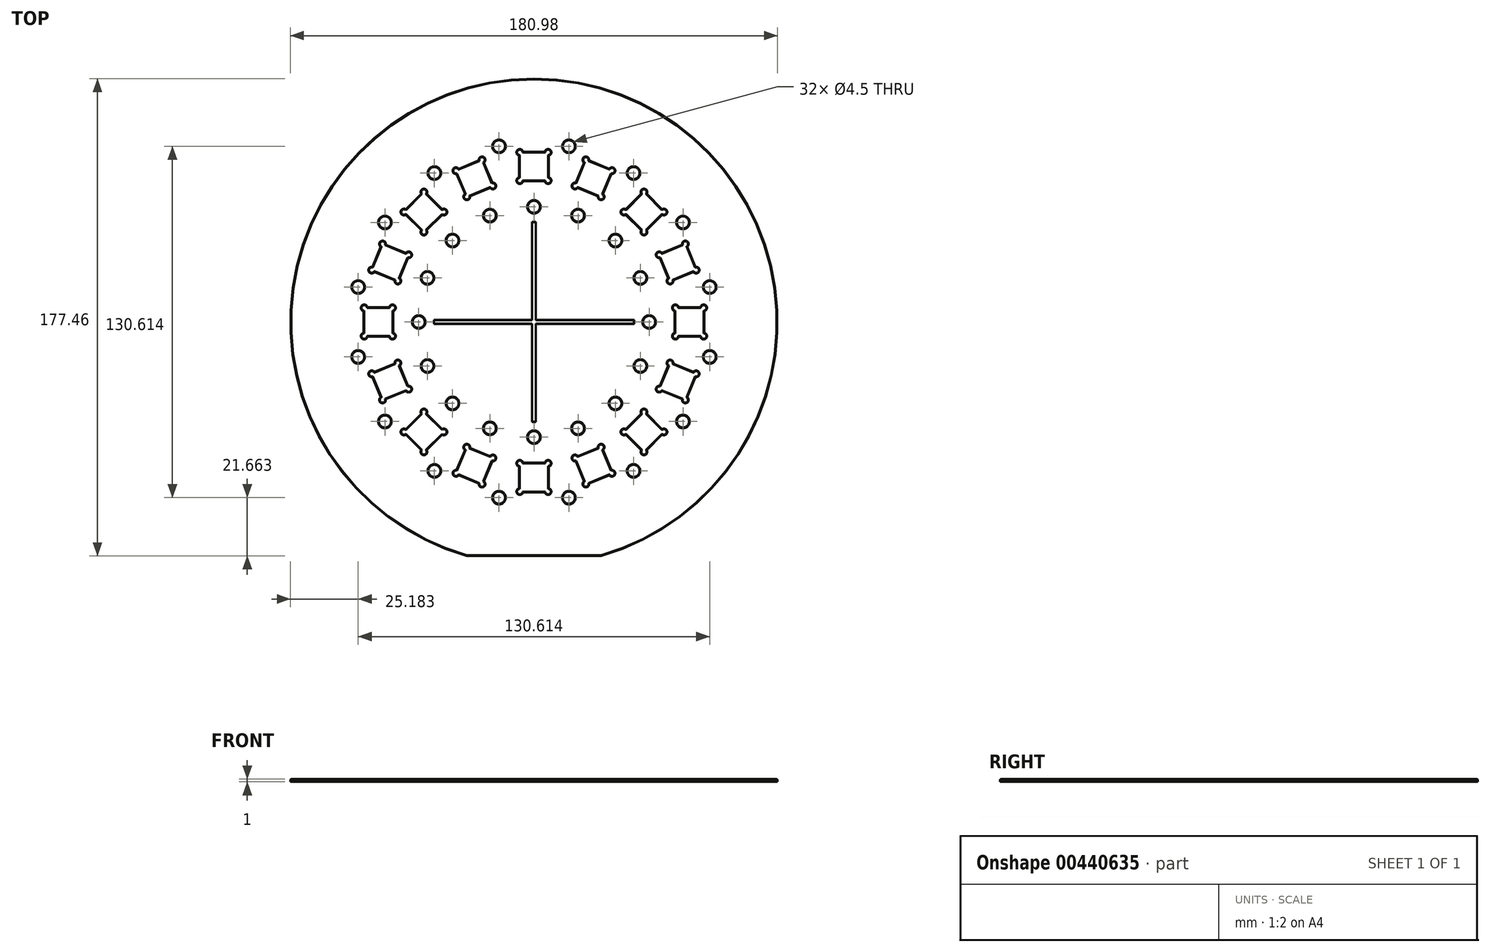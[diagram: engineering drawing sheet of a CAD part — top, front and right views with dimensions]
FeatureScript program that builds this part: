
annotation { "Feature Type Name" : "Feature", "Feature Type Description" : "" }
export const myFeature = defineFeature(function(context is Context, id is Id, definition is map)
    precondition{}
    {
        {
            var Q0;
            Q0=qCreatedBy(makeId("Top.planeOp"),FACE);
            var sketch = newSketch(context, id + "F0", { "sketchPlane" : qUnion([Q0])});
            skArc(sketch, "E0", {"start": v(25, -86.97) * mm, "mid": v(0, 90.49) * mm, "end": v(-25, -86.97) * mm});
            skCircle(sketch, "E1", {"center": v(0, 0) * mm, "radius": 57.8 * mm, "construction": true});
            skLineSegment(sketch, "E2.bottom", {"start": v(5.25, 63.06) * mm, "end": v(-5.25, 63.06) * mm});
            skLineSegment(sketch, "E2.top", {"start": v(5.25, 52.56) * mm, "end": v(-5.25, 52.56) * mm});
            skLineSegment(sketch, "E2.left", {"start": v(5.25, 63.06) * mm, "end": v(5.25, 52.56) * mm});
            skLineSegment(sketch, "E2.right", {"start": v(-5.25, 63.06) * mm, "end": v(-5.25, 52.56) * mm});
            skPoint(sketch, "E2.middle", {"position": v(0, 57.8) * mm});
            skCircle(sketch, "E3", {"center": v(0, 42.8) * mm, "radius": 2.25 * mm});
            skLineSegment(sketch, "E4", {"start": v(0, 42.8) * mm, "end": v(0, 57.8) * mm, "construction": true});
            skCircle(sketch, "E5.1.0", {"center": v(13, 65.3) * mm, "radius": 2.25 * mm, "construction": true});
            skCircle(sketch, "E5.2.0", {"center": v(-13, 65.3) * mm, "radius": 2.25 * mm});
            skCircle(sketch, "E6", {"center": v(-5.25, 63.06) * mm, "radius": 1 * mm});
            skCircle(sketch, "E7", {"center": v(5.25, 63.06) * mm, "radius": 1 * mm});
            skCircle(sketch, "E8", {"center": v(5.25, 52.56) * mm, "radius": 1 * mm});
            skCircle(sketch, "E9", {"center": v(-5.25, 52.56) * mm, "radius": 1 * mm});
            skLineSegment(sketch, "E10.1.0", {"start": v(-19.28, 60.27) * mm, "end": v(-15.26, 50.57) * mm});
            skLineSegment(sketch, "E10.1.1", {"start": v(-28.98, 56.25) * mm, "end": v(-24.96, 46.55) * mm});
            skPoint(sketch, "E10.1.2", {"position": v(-22.12, 53.4) * mm});
            skCircle(sketch, "E10.1.3", {"center": v(-16.38, 39.55) * mm, "radius": 2.25 * mm});
            skLineSegment(sketch, "E10.1.4", {"start": v(-15.26, 50.57) * mm, "end": v(-24.96, 46.55) * mm});
            skCircle(sketch, "E10.1.5", {"center": v(-13, 65.3) * mm, "radius": 2.25 * mm, "construction": true});
            skLineSegment(sketch, "E10.1.6", {"start": v(-16.38, 39.55) * mm, "end": v(-22.12, 53.4) * mm, "construction": true});
            skCircle(sketch, "E10.1.7", {"center": v(-37, 55.36) * mm, "radius": 2.25 * mm});
            skLineSegment(sketch, "E10.1.8", {"start": v(-19.28, 60.27) * mm, "end": v(-28.98, 56.25) * mm});
            skPoint(sketch, "E10.1.9", {"position": v(-22.12, 53.4) * mm});
            skCircle(sketch, "E10.1.10", {"center": v(-19.28, 60.27) * mm, "radius": 1 * mm});
            skCircle(sketch, "E10.1.11", {"center": v(-15.26, 50.57) * mm, "radius": 1 * mm});
            skCircle(sketch, "E10.1.12", {"center": v(-24.96, 46.55) * mm, "radius": 1 * mm});
            skCircle(sketch, "E10.1.13", {"center": v(-28.98, 56.25) * mm, "radius": 1 * mm});
            skLineSegment(sketch, "E10.2.0", {"start": v(-40.88, 48.3) * mm, "end": v(-33.45, 40.88) * mm});
            skLineSegment(sketch, "E10.2.1", {"start": v(-48.3, 40.88) * mm, "end": v(-40.88, 33.45) * mm});
            skPoint(sketch, "E10.2.2", {"position": v(-40.88, 40.88) * mm});
            skCircle(sketch, "E10.2.3", {"center": v(-30.27, 30.27) * mm, "radius": 2.25 * mm});
            skLineSegment(sketch, "E10.2.4", {"start": v(-33.45, 40.88) * mm, "end": v(-40.88, 33.45) * mm});
            skCircle(sketch, "E10.2.5", {"center": v(-37, 55.36) * mm, "radius": 2.25 * mm, "construction": true});
            skLineSegment(sketch, "E10.2.6", {"start": v(-30.27, 30.27) * mm, "end": v(-40.88, 40.88) * mm, "construction": true});
            skCircle(sketch, "E10.2.7", {"center": v(-55.36, 37) * mm, "radius": 2.25 * mm});
            skLineSegment(sketch, "E10.2.8", {"start": v(-40.88, 48.3) * mm, "end": v(-48.3, 40.88) * mm});
            skPoint(sketch, "E10.2.9", {"position": v(-40.88, 40.88) * mm});
            skCircle(sketch, "E10.2.10", {"center": v(-40.88, 48.3) * mm, "radius": 1 * mm});
            skCircle(sketch, "E10.2.11", {"center": v(-33.45, 40.88) * mm, "radius": 1 * mm});
            skCircle(sketch, "E10.2.12", {"center": v(-40.88, 33.45) * mm, "radius": 1 * mm});
            skCircle(sketch, "E10.2.13", {"center": v(-48.3, 40.88) * mm, "radius": 1 * mm});
            skLineSegment(sketch, "E11.3.3.0", {"start": v(-60.27, 19.28) * mm, "end": v(-50.57, 15.26) * mm});
            skPoint(sketch, "E11.6.3.0", {"position": v(-53.4, 22.12) * mm});
            skCircle(sketch, "E11.7.3.0", {"center": v(-39.55, 16.38) * mm, "radius": 2.25 * mm});
            skLineSegment(sketch, "E11.8.3.0", {"start": v(-56.25, 28.98) * mm, "end": v(-46.55, 24.96) * mm});
            skLineSegment(sketch, "E11.9.3.0", {"start": v(-46.55, 24.96) * mm, "end": v(-50.57, 15.26) * mm});
            skCircle(sketch, "E11.12.3.0", {"center": v(-55.36, 37) * mm, "radius": 2.25 * mm, "construction": true});
            skLineSegment(sketch, "E11.14.3.0", {"start": v(-39.55, 16.38) * mm, "end": v(-53.4, 22.12) * mm, "construction": true});
            skCircle(sketch, "E11.17.3.0", {"center": v(-65.3, 13) * mm, "radius": 2.25 * mm});
            skLineSegment(sketch, "E11.19.3.0", {"start": v(-56.25, 28.98) * mm, "end": v(-60.27, 19.28) * mm});
            skPoint(sketch, "E11.22.3.0", {"position": v(-53.4, 22.12) * mm});
            skCircle(sketch, "E11.23.3.0", {"center": v(-56.25, 28.98) * mm, "radius": 1 * mm});
            skCircle(sketch, "E11.25.3.0", {"center": v(-46.55, 24.96) * mm, "radius": 1 * mm});
            skCircle(sketch, "E11.27.3.0", {"center": v(-50.57, 15.26) * mm, "radius": 1 * mm});
            skCircle(sketch, "E11.29.3.0", {"center": v(-60.27, 19.28) * mm, "radius": 1 * mm});
            skLineSegment(sketch, "E11.3.4.0", {"start": v(-63.06, -5.25) * mm, "end": v(-52.56, -5.25) * mm});
            skPoint(sketch, "E11.6.4.0", {"position": v(-57.8, 0) * mm});
            skCircle(sketch, "E11.7.4.0", {"center": v(-42.8, 0) * mm, "radius": 2.25 * mm});
            skLineSegment(sketch, "E11.8.4.0", {"start": v(-63.06, 5.25) * mm, "end": v(-52.56, 5.25) * mm});
            skLineSegment(sketch, "E11.9.4.0", {"start": v(-52.56, 5.25) * mm, "end": v(-52.56, -5.25) * mm});
            skCircle(sketch, "E11.12.4.0", {"center": v(-65.3, 13) * mm, "radius": 2.25 * mm, "construction": true});
            skLineSegment(sketch, "E11.14.4.0", {"start": v(-42.8, 0) * mm, "end": v(-57.8, 0) * mm, "construction": true});
            skCircle(sketch, "E11.17.4.0", {"center": v(-65.3, -13) * mm, "radius": 2.25 * mm});
            skLineSegment(sketch, "E11.19.4.0", {"start": v(-63.06, 5.25) * mm, "end": v(-63.06, -5.25) * mm});
            skPoint(sketch, "E11.22.4.0", {"position": v(-57.8, 0) * mm});
            skCircle(sketch, "E11.23.4.0", {"center": v(-63.06, 5.25) * mm, "radius": 1 * mm});
            skCircle(sketch, "E11.25.4.0", {"center": v(-52.56, 5.25) * mm, "radius": 1 * mm});
            skCircle(sketch, "E11.27.4.0", {"center": v(-52.56, -5.25) * mm, "radius": 1 * mm});
            skCircle(sketch, "E11.29.4.0", {"center": v(-63.06, -5.25) * mm, "radius": 1 * mm});
            skLineSegment(sketch, "E11.3.5.0", {"start": v(-56.25, -28.98) * mm, "end": v(-46.55, -24.96) * mm});
            skPoint(sketch, "E11.6.5.0", {"position": v(-53.4, -22.12) * mm});
            skCircle(sketch, "E11.7.5.0", {"center": v(-39.55, -16.38) * mm, "radius": 2.25 * mm});
            skLineSegment(sketch, "E11.8.5.0", {"start": v(-60.27, -19.28) * mm, "end": v(-50.57, -15.26) * mm});
            skLineSegment(sketch, "E11.9.5.0", {"start": v(-50.57, -15.26) * mm, "end": v(-46.55, -24.96) * mm});
            skCircle(sketch, "E11.12.5.0", {"center": v(-65.3, -13) * mm, "radius": 2.25 * mm, "construction": true});
            skLineSegment(sketch, "E11.14.5.0", {"start": v(-39.55, -16.38) * mm, "end": v(-53.4, -22.12) * mm, "construction": true});
            skCircle(sketch, "E11.17.5.0", {"center": v(-55.36, -37) * mm, "radius": 2.25 * mm});
            skLineSegment(sketch, "E11.19.5.0", {"start": v(-60.27, -19.28) * mm, "end": v(-56.25, -28.98) * mm});
            skPoint(sketch, "E11.22.5.0", {"position": v(-53.4, -22.12) * mm});
            skCircle(sketch, "E11.23.5.0", {"center": v(-60.27, -19.28) * mm, "radius": 1 * mm});
            skCircle(sketch, "E11.25.5.0", {"center": v(-50.57, -15.26) * mm, "radius": 1 * mm});
            skCircle(sketch, "E11.27.5.0", {"center": v(-46.55, -24.96) * mm, "radius": 1 * mm});
            skCircle(sketch, "E11.29.5.0", {"center": v(-56.25, -28.98) * mm, "radius": 1 * mm});
            skLineSegment(sketch, "E11.3.6.0", {"start": v(-40.88, -48.3) * mm, "end": v(-33.45, -40.88) * mm});
            skPoint(sketch, "E11.6.6.0", {"position": v(-40.88, -40.88) * mm});
            skCircle(sketch, "E11.7.6.0", {"center": v(-30.27, -30.27) * mm, "radius": 2.25 * mm});
            skLineSegment(sketch, "E11.8.6.0", {"start": v(-48.3, -40.88) * mm, "end": v(-40.88, -33.45) * mm});
            skLineSegment(sketch, "E11.9.6.0", {"start": v(-40.88, -33.45) * mm, "end": v(-33.45, -40.88) * mm});
            skCircle(sketch, "E11.12.6.0", {"center": v(-55.36, -37) * mm, "radius": 2.25 * mm, "construction": true});
            skLineSegment(sketch, "E11.14.6.0", {"start": v(-30.27, -30.27) * mm, "end": v(-40.88, -40.88) * mm, "construction": true});
            skCircle(sketch, "E11.17.6.0", {"center": v(-37, -55.36) * mm, "radius": 2.25 * mm});
            skLineSegment(sketch, "E11.19.6.0", {"start": v(-48.3, -40.88) * mm, "end": v(-40.88, -48.3) * mm});
            skPoint(sketch, "E11.22.6.0", {"position": v(-40.88, -40.88) * mm});
            skCircle(sketch, "E11.23.6.0", {"center": v(-48.3, -40.88) * mm, "radius": 1 * mm});
            skCircle(sketch, "E11.25.6.0", {"center": v(-40.88, -33.45) * mm, "radius": 1 * mm});
            skCircle(sketch, "E11.27.6.0", {"center": v(-33.45, -40.88) * mm, "radius": 1 * mm});
            skCircle(sketch, "E11.29.6.0", {"center": v(-40.88, -48.3) * mm, "radius": 1 * mm});
            skLineSegment(sketch, "E11.3.7.0", {"start": v(-19.28, -60.27) * mm, "end": v(-15.26, -50.57) * mm});
            skPoint(sketch, "E11.6.7.0", {"position": v(-22.12, -53.4) * mm});
            skCircle(sketch, "E11.7.7.0", {"center": v(-16.38, -39.55) * mm, "radius": 2.25 * mm});
            skLineSegment(sketch, "E11.8.7.0", {"start": v(-28.98, -56.25) * mm, "end": v(-24.96, -46.55) * mm});
            skLineSegment(sketch, "E11.9.7.0", {"start": v(-24.96, -46.55) * mm, "end": v(-15.26, -50.57) * mm});
            skCircle(sketch, "E11.12.7.0", {"center": v(-37, -55.36) * mm, "radius": 2.25 * mm, "construction": true});
            skLineSegment(sketch, "E11.14.7.0", {"start": v(-16.38, -39.55) * mm, "end": v(-22.12, -53.4) * mm, "construction": true});
            skCircle(sketch, "E11.17.7.0", {"center": v(-13, -65.3) * mm, "radius": 2.25 * mm});
            skLineSegment(sketch, "E11.19.7.0", {"start": v(-28.98, -56.25) * mm, "end": v(-19.28, -60.27) * mm});
            skPoint(sketch, "E11.22.7.0", {"position": v(-22.12, -53.4) * mm});
            skCircle(sketch, "E11.23.7.0", {"center": v(-28.98, -56.25) * mm, "radius": 1 * mm});
            skCircle(sketch, "E11.25.7.0", {"center": v(-24.96, -46.55) * mm, "radius": 1 * mm});
            skCircle(sketch, "E11.27.7.0", {"center": v(-15.26, -50.57) * mm, "radius": 1 * mm});
            skCircle(sketch, "E11.29.7.0", {"center": v(-19.28, -60.27) * mm, "radius": 1 * mm});
            skLineSegment(sketch, "E11.3.8.0", {"start": v(5.25, -63.06) * mm, "end": v(5.25, -52.56) * mm});
            skPoint(sketch, "E11.6.8.0", {"position": v(0, -57.8) * mm});
            skCircle(sketch, "E11.7.8.0", {"center": v(0, -42.8) * mm, "radius": 2.25 * mm});
            skLineSegment(sketch, "E11.8.8.0", {"start": v(-5.25, -63.06) * mm, "end": v(-5.25, -52.56) * mm});
            skLineSegment(sketch, "E11.9.8.0", {"start": v(-5.25, -52.56) * mm, "end": v(5.25, -52.56) * mm});
            skCircle(sketch, "E11.12.8.0", {"center": v(-13, -65.3) * mm, "radius": 2.25 * mm, "construction": true});
            skLineSegment(sketch, "E11.14.8.0", {"start": v(0, -42.8) * mm, "end": v(0, -57.8) * mm, "construction": true});
            skCircle(sketch, "E11.17.8.0", {"center": v(13, -65.3) * mm, "radius": 2.25 * mm});
            skLineSegment(sketch, "E11.19.8.0", {"start": v(-5.25, -63.06) * mm, "end": v(5.25, -63.06) * mm});
            skPoint(sketch, "E11.22.8.0", {"position": v(0, -57.8) * mm});
            skCircle(sketch, "E11.23.8.0", {"center": v(-5.25, -63.06) * mm, "radius": 1 * mm});
            skCircle(sketch, "E11.25.8.0", {"center": v(-5.25, -52.56) * mm, "radius": 1 * mm});
            skCircle(sketch, "E11.27.8.0", {"center": v(5.25, -52.56) * mm, "radius": 1 * mm});
            skCircle(sketch, "E11.29.8.0", {"center": v(5.25, -63.06) * mm, "radius": 1 * mm});
            skLineSegment(sketch, "E11.3.9.0", {"start": v(28.98, -56.25) * mm, "end": v(24.96, -46.55) * mm});
            skPoint(sketch, "E11.6.9.0", {"position": v(22.12, -53.4) * mm});
            skCircle(sketch, "E11.7.9.0", {"center": v(16.38, -39.55) * mm, "radius": 2.25 * mm});
            skLineSegment(sketch, "E11.8.9.0", {"start": v(19.28, -60.27) * mm, "end": v(15.26, -50.57) * mm});
            skLineSegment(sketch, "E11.9.9.0", {"start": v(15.26, -50.57) * mm, "end": v(24.96, -46.55) * mm});
            skCircle(sketch, "E11.12.9.0", {"center": v(13, -65.3) * mm, "radius": 2.25 * mm, "construction": true});
            skLineSegment(sketch, "E11.14.9.0", {"start": v(16.38, -39.55) * mm, "end": v(22.12, -53.4) * mm, "construction": true});
            skCircle(sketch, "E11.17.9.0", {"center": v(37, -55.36) * mm, "radius": 2.25 * mm});
            skLineSegment(sketch, "E11.19.9.0", {"start": v(19.28, -60.27) * mm, "end": v(28.98, -56.25) * mm});
            skPoint(sketch, "E11.22.9.0", {"position": v(22.12, -53.4) * mm});
            skCircle(sketch, "E11.23.9.0", {"center": v(19.28, -60.27) * mm, "radius": 1 * mm});
            skCircle(sketch, "E11.25.9.0", {"center": v(15.26, -50.57) * mm, "radius": 1 * mm});
            skCircle(sketch, "E11.27.9.0", {"center": v(24.96, -46.55) * mm, "radius": 1 * mm});
            skCircle(sketch, "E11.29.9.0", {"center": v(28.98, -56.25) * mm, "radius": 1 * mm});
            skLineSegment(sketch, "E11.3.10.0", {"start": v(48.3, -40.88) * mm, "end": v(40.88, -33.45) * mm});
            skPoint(sketch, "E11.6.10.0", {"position": v(40.88, -40.88) * mm});
            skCircle(sketch, "E11.7.10.0", {"center": v(30.27, -30.27) * mm, "radius": 2.25 * mm});
            skLineSegment(sketch, "E11.8.10.0", {"start": v(40.88, -48.3) * mm, "end": v(33.45, -40.88) * mm});
            skLineSegment(sketch, "E11.9.10.0", {"start": v(33.45, -40.88) * mm, "end": v(40.88, -33.45) * mm});
            skCircle(sketch, "E11.12.10.0", {"center": v(37, -55.36) * mm, "radius": 2.25 * mm, "construction": true});
            skLineSegment(sketch, "E11.14.10.0", {"start": v(30.27, -30.27) * mm, "end": v(40.88, -40.88) * mm, "construction": true});
            skCircle(sketch, "E11.17.10.0", {"center": v(55.36, -37) * mm, "radius": 2.25 * mm});
            skLineSegment(sketch, "E11.19.10.0", {"start": v(40.88, -48.3) * mm, "end": v(48.3, -40.88) * mm});
            skPoint(sketch, "E11.22.10.0", {"position": v(40.88, -40.88) * mm});
            skCircle(sketch, "E11.23.10.0", {"center": v(40.88, -48.3) * mm, "radius": 1 * mm});
            skCircle(sketch, "E11.25.10.0", {"center": v(33.45, -40.88) * mm, "radius": 1 * mm});
            skCircle(sketch, "E11.27.10.0", {"center": v(40.88, -33.45) * mm, "radius": 1 * mm});
            skCircle(sketch, "E11.29.10.0", {"center": v(48.3, -40.88) * mm, "radius": 1 * mm});
            skLineSegment(sketch, "E11.3.11.0", {"start": v(60.27, -19.28) * mm, "end": v(50.57, -15.26) * mm});
            skPoint(sketch, "E11.6.11.0", {"position": v(53.4, -22.12) * mm});
            skCircle(sketch, "E11.7.11.0", {"center": v(39.55, -16.38) * mm, "radius": 2.25 * mm});
            skLineSegment(sketch, "E11.8.11.0", {"start": v(56.25, -28.98) * mm, "end": v(46.55, -24.96) * mm});
            skLineSegment(sketch, "E11.9.11.0", {"start": v(46.55, -24.96) * mm, "end": v(50.57, -15.26) * mm});
            skCircle(sketch, "E11.12.11.0", {"center": v(55.36, -37) * mm, "radius": 2.25 * mm, "construction": true});
            skLineSegment(sketch, "E11.14.11.0", {"start": v(39.55, -16.38) * mm, "end": v(53.4, -22.12) * mm, "construction": true});
            skCircle(sketch, "E11.17.11.0", {"center": v(65.3, -13) * mm, "radius": 2.25 * mm});
            skLineSegment(sketch, "E11.19.11.0", {"start": v(56.25, -28.98) * mm, "end": v(60.27, -19.28) * mm});
            skPoint(sketch, "E11.22.11.0", {"position": v(53.4, -22.12) * mm});
            skCircle(sketch, "E11.23.11.0", {"center": v(56.25, -28.98) * mm, "radius": 1 * mm});
            skCircle(sketch, "E11.25.11.0", {"center": v(46.55, -24.96) * mm, "radius": 1 * mm});
            skCircle(sketch, "E11.27.11.0", {"center": v(50.57, -15.26) * mm, "radius": 1 * mm});
            skCircle(sketch, "E11.29.11.0", {"center": v(60.27, -19.28) * mm, "radius": 1 * mm});
            skLineSegment(sketch, "E11.3.12.0", {"start": v(63.06, 5.25) * mm, "end": v(52.56, 5.25) * mm});
            skPoint(sketch, "E11.6.12.0", {"position": v(57.8, 0) * mm});
            skCircle(sketch, "E11.7.12.0", {"center": v(42.8, 0) * mm, "radius": 2.25 * mm});
            skLineSegment(sketch, "E11.8.12.0", {"start": v(63.06, -5.25) * mm, "end": v(52.56, -5.25) * mm});
            skLineSegment(sketch, "E11.9.12.0", {"start": v(52.56, -5.25) * mm, "end": v(52.56, 5.25) * mm});
            skCircle(sketch, "E11.12.12.0", {"center": v(65.3, -13) * mm, "radius": 2.25 * mm, "construction": true});
            skLineSegment(sketch, "E11.14.12.0", {"start": v(42.8, 0) * mm, "end": v(57.8, 0) * mm, "construction": true});
            skCircle(sketch, "E11.17.12.0", {"center": v(65.3, 13) * mm, "radius": 2.25 * mm});
            skLineSegment(sketch, "E11.19.12.0", {"start": v(63.06, -5.25) * mm, "end": v(63.06, 5.25) * mm});
            skPoint(sketch, "E11.22.12.0", {"position": v(57.8, 0) * mm});
            skCircle(sketch, "E11.23.12.0", {"center": v(63.06, -5.25) * mm, "radius": 1 * mm});
            skCircle(sketch, "E11.25.12.0", {"center": v(52.56, -5.25) * mm, "radius": 1 * mm});
            skCircle(sketch, "E11.27.12.0", {"center": v(52.56, 5.25) * mm, "radius": 1 * mm});
            skCircle(sketch, "E11.29.12.0", {"center": v(63.06, 5.25) * mm, "radius": 1 * mm});
            skLineSegment(sketch, "E11.3.13.0", {"start": v(56.25, 28.98) * mm, "end": v(46.55, 24.96) * mm});
            skPoint(sketch, "E11.6.13.0", {"position": v(53.4, 22.12) * mm});
            skCircle(sketch, "E11.7.13.0", {"center": v(39.55, 16.38) * mm, "radius": 2.25 * mm});
            skLineSegment(sketch, "E11.8.13.0", {"start": v(60.27, 19.28) * mm, "end": v(50.57, 15.26) * mm});
            skLineSegment(sketch, "E11.9.13.0", {"start": v(50.57, 15.26) * mm, "end": v(46.55, 24.96) * mm});
            skCircle(sketch, "E11.12.13.0", {"center": v(65.3, 13) * mm, "radius": 2.25 * mm, "construction": true});
            skLineSegment(sketch, "E11.14.13.0", {"start": v(39.55, 16.38) * mm, "end": v(53.4, 22.12) * mm, "construction": true});
            skCircle(sketch, "E11.17.13.0", {"center": v(55.36, 37) * mm, "radius": 2.25 * mm});
            skLineSegment(sketch, "E11.19.13.0", {"start": v(60.27, 19.28) * mm, "end": v(56.25, 28.98) * mm});
            skPoint(sketch, "E11.22.13.0", {"position": v(53.4, 22.12) * mm});
            skCircle(sketch, "E11.23.13.0", {"center": v(60.27, 19.28) * mm, "radius": 1 * mm});
            skCircle(sketch, "E11.25.13.0", {"center": v(50.57, 15.26) * mm, "radius": 1 * mm});
            skCircle(sketch, "E11.27.13.0", {"center": v(46.55, 24.96) * mm, "radius": 1 * mm});
            skCircle(sketch, "E11.29.13.0", {"center": v(56.25, 28.98) * mm, "radius": 1 * mm});
            skLineSegment(sketch, "E11.3.14.0", {"start": v(40.88, 48.3) * mm, "end": v(33.45, 40.88) * mm});
            skPoint(sketch, "E11.6.14.0", {"position": v(40.88, 40.88) * mm});
            skCircle(sketch, "E11.7.14.0", {"center": v(30.27, 30.27) * mm, "radius": 2.25 * mm});
            skLineSegment(sketch, "E11.8.14.0", {"start": v(48.3, 40.88) * mm, "end": v(40.88, 33.45) * mm});
            skLineSegment(sketch, "E11.9.14.0", {"start": v(40.88, 33.45) * mm, "end": v(33.45, 40.88) * mm});
            skCircle(sketch, "E11.12.14.0", {"center": v(55.36, 37) * mm, "radius": 2.25 * mm, "construction": true});
            skLineSegment(sketch, "E11.14.14.0", {"start": v(30.27, 30.27) * mm, "end": v(40.88, 40.88) * mm, "construction": true});
            skCircle(sketch, "E11.17.14.0", {"center": v(37, 55.36) * mm, "radius": 2.25 * mm});
            skLineSegment(sketch, "E11.19.14.0", {"start": v(48.3, 40.88) * mm, "end": v(40.88, 48.3) * mm});
            skPoint(sketch, "E11.22.14.0", {"position": v(40.88, 40.88) * mm});
            skCircle(sketch, "E11.23.14.0", {"center": v(48.3, 40.88) * mm, "radius": 1 * mm});
            skCircle(sketch, "E11.25.14.0", {"center": v(40.88, 33.45) * mm, "radius": 1 * mm});
            skCircle(sketch, "E11.27.14.0", {"center": v(33.45, 40.88) * mm, "radius": 1 * mm});
            skCircle(sketch, "E11.29.14.0", {"center": v(40.88, 48.3) * mm, "radius": 1 * mm});
            skLineSegment(sketch, "E11.3.15.0", {"start": v(19.28, 60.27) * mm, "end": v(15.26, 50.57) * mm});
            skPoint(sketch, "E11.6.15.0", {"position": v(22.12, 53.4) * mm});
            skCircle(sketch, "E11.7.15.0", {"center": v(16.38, 39.55) * mm, "radius": 2.25 * mm});
            skLineSegment(sketch, "E11.8.15.0", {"start": v(28.98, 56.25) * mm, "end": v(24.96, 46.55) * mm});
            skLineSegment(sketch, "E11.9.15.0", {"start": v(24.96, 46.55) * mm, "end": v(15.26, 50.57) * mm});
            skCircle(sketch, "E11.12.15.0", {"center": v(37, 55.36) * mm, "radius": 2.25 * mm, "construction": true});
            skLineSegment(sketch, "E11.14.15.0", {"start": v(16.38, 39.55) * mm, "end": v(22.12, 53.4) * mm, "construction": true});
            skCircle(sketch, "E11.17.15.0", {"center": v(13, 65.3) * mm, "radius": 2.25 * mm});
            skLineSegment(sketch, "E11.19.15.0", {"start": v(28.98, 56.25) * mm, "end": v(19.28, 60.27) * mm});
            skPoint(sketch, "E11.22.15.0", {"position": v(22.12, 53.4) * mm});
            skCircle(sketch, "E11.23.15.0", {"center": v(28.98, 56.25) * mm, "radius": 1 * mm});
            skCircle(sketch, "E11.25.15.0", {"center": v(24.96, 46.55) * mm, "radius": 1 * mm});
            skCircle(sketch, "E11.27.15.0", {"center": v(15.26, 50.57) * mm, "radius": 1 * mm});
            skCircle(sketch, "E11.29.15.0", {"center": v(19.28, 60.27) * mm, "radius": 1 * mm});
            skLineSegment(sketch, "E12", {"start": v(-25, -86.97) * mm, "end": v(25, -86.97) * mm});
            skLineSegment(sketch, "E13", {"start": v(0, 0) * mm, "end": v(0, -86.97) * mm, "construction": true});
            skPoint(sketch, "E13.endSnap0", {"position": v(0, -50.3) * mm});
            skSolve(sketch);
        }
        {
            var Q0;
            Q0 = qSketchRegion(id + "F0", true);
            extrude(context, id + "F1", {"entities" : qUnion([Q0]), "depth" : 1 * mm});
        }
        {
            var Q0;
            Q0=makeQuery(id+"F1.opExtrude","CAP_FACE",FACE,{"disambiguationData":[OSD([sQuery(id+"F0.wireOp",EDGE,"E0"),sQuery(id+"F0.wireOp",EDGE,"E2.bottom"),sQuery(id+"F0.wireOp",EDGE,"E2.top"),sQuery(id+"F0.wireOp",EDGE,"E2.left"),sQuery(id+"F0.wireOp",EDGE,"E2.right"),sQuery(id+"F0.wireOp",EDGE,"E3"),sQuery(id+"F0.wireOp",EDGE,"E5.2.0"),sQuery(id+"F0.wireOp",EDGE,"E6"),sQuery(id+"F0.wireOp",EDGE,"E7"),sQuery(id+"F0.wireOp",EDGE,"E8"),sQuery(id+"F0.wireOp",EDGE,"E9"),sQuery(id+"F0.wireOp",EDGE,"E10.1.0"),sQuery(id+"F0.wireOp",EDGE,"E10.1.1"),sQuery(id+"F0.wireOp",EDGE,"E10.1.3"),sQuery(id+"F0.wireOp",EDGE,"E10.1.4"),sQuery(id+"F0.wireOp",EDGE,"E10.1.7"),sQuery(id+"F0.wireOp",EDGE,"E10.1.8"),sQuery(id+"F0.wireOp",EDGE,"E10.1.10"),sQuery(id+"F0.wireOp",EDGE,"E10.1.11"),sQuery(id+"F0.wireOp",EDGE,"E10.1.12"),sQuery(id+"F0.wireOp",EDGE,"E10.1.13"),sQuery(id+"F0.wireOp",EDGE,"E10.2.0"),sQuery(id+"F0.wireOp",EDGE,"E10.2.1"),sQuery(id+"F0.wireOp",EDGE,"E10.2.3"),sQuery(id+"F0.wireOp",EDGE,"E10.2.4"),sQuery(id+"F0.wireOp",EDGE,"E10.2.7"),sQuery(id+"F0.wireOp",EDGE,"E10.2.8"),sQuery(id+"F0.wireOp",EDGE,"E10.2.10"),sQuery(id+"F0.wireOp",EDGE,"E10.2.11"),sQuery(id+"F0.wireOp",EDGE,"E10.2.12"),sQuery(id+"F0.wireOp",EDGE,"E10.2.13"),sQuery(id+"F0.wireOp",EDGE,"E11.3.3.0"),sQuery(id+"F0.wireOp",EDGE,"E11.7.3.0"),sQuery(id+"F0.wireOp",EDGE,"E11.8.3.0"),sQuery(id+"F0.wireOp",EDGE,"E11.9.3.0"),sQuery(id+"F0.wireOp",EDGE,"E11.17.3.0"),sQuery(id+"F0.wireOp",EDGE,"E11.19.3.0"),sQuery(id+"F0.wireOp",EDGE,"E11.23.3.0"),sQuery(id+"F0.wireOp",EDGE,"E11.25.3.0"),sQuery(id+"F0.wireOp",EDGE,"E11.27.3.0"),sQuery(id+"F0.wireOp",EDGE,"E11.29.3.0"),sQuery(id+"F0.wireOp",EDGE,"E11.3.4.0"),sQuery(id+"F0.wireOp",EDGE,"E11.7.4.0"),sQuery(id+"F0.wireOp",EDGE,"E11.8.4.0"),sQuery(id+"F0.wireOp",EDGE,"E11.9.4.0"),sQuery(id+"F0.wireOp",EDGE,"E11.17.4.0"),sQuery(id+"F0.wireOp",EDGE,"E11.19.4.0"),sQuery(id+"F0.wireOp",EDGE,"E11.23.4.0"),sQuery(id+"F0.wireOp",EDGE,"E11.25.4.0"),sQuery(id+"F0.wireOp",EDGE,"E11.27.4.0"),sQuery(id+"F0.wireOp",EDGE,"E11.29.4.0"),sQuery(id+"F0.wireOp",EDGE,"E11.3.5.0"),sQuery(id+"F0.wireOp",EDGE,"E11.7.5.0"),sQuery(id+"F0.wireOp",EDGE,"E11.8.5.0"),sQuery(id+"F0.wireOp",EDGE,"E11.9.5.0"),sQuery(id+"F0.wireOp",EDGE,"E11.17.5.0"),sQuery(id+"F0.wireOp",EDGE,"E11.19.5.0"),sQuery(id+"F0.wireOp",EDGE,"E11.23.5.0"),sQuery(id+"F0.wireOp",EDGE,"E11.25.5.0"),sQuery(id+"F0.wireOp",EDGE,"E11.27.5.0"),sQuery(id+"F0.wireOp",EDGE,"E11.29.5.0"),sQuery(id+"F0.wireOp",EDGE,"E11.3.6.0"),sQuery(id+"F0.wireOp",EDGE,"E11.7.6.0"),sQuery(id+"F0.wireOp",EDGE,"E11.8.6.0"),sQuery(id+"F0.wireOp",EDGE,"E11.9.6.0"),sQuery(id+"F0.wireOp",EDGE,"E11.17.6.0"),sQuery(id+"F0.wireOp",EDGE,"E11.19.6.0"),sQuery(id+"F0.wireOp",EDGE,"E11.23.6.0"),sQuery(id+"F0.wireOp",EDGE,"E11.25.6.0"),sQuery(id+"F0.wireOp",EDGE,"E11.27.6.0"),sQuery(id+"F0.wireOp",EDGE,"E11.29.6.0"),sQuery(id+"F0.wireOp",EDGE,"E11.3.7.0"),sQuery(id+"F0.wireOp",EDGE,"E11.7.7.0"),sQuery(id+"F0.wireOp",EDGE,"E11.8.7.0"),sQuery(id+"F0.wireOp",EDGE,"E11.9.7.0"),sQuery(id+"F0.wireOp",EDGE,"E11.17.7.0"),sQuery(id+"F0.wireOp",EDGE,"E11.19.7.0"),sQuery(id+"F0.wireOp",EDGE,"E11.23.7.0"),sQuery(id+"F0.wireOp",EDGE,"E11.25.7.0"),sQuery(id+"F0.wireOp",EDGE,"E11.27.7.0"),sQuery(id+"F0.wireOp",EDGE,"E11.29.7.0"),sQuery(id+"F0.wireOp",EDGE,"E11.3.8.0"),sQuery(id+"F0.wireOp",EDGE,"E11.7.8.0"),sQuery(id+"F0.wireOp",EDGE,"E11.8.8.0"),sQuery(id+"F0.wireOp",EDGE,"E11.9.8.0"),sQuery(id+"F0.wireOp",EDGE,"E11.17.8.0"),sQuery(id+"F0.wireOp",EDGE,"E11.19.8.0"),sQuery(id+"F0.wireOp",EDGE,"E11.23.8.0"),sQuery(id+"F0.wireOp",EDGE,"E11.25.8.0"),sQuery(id+"F0.wireOp",EDGE,"E11.27.8.0"),sQuery(id+"F0.wireOp",EDGE,"E11.29.8.0"),sQuery(id+"F0.wireOp",EDGE,"E11.3.9.0"),sQuery(id+"F0.wireOp",EDGE,"E11.7.9.0"),sQuery(id+"F0.wireOp",EDGE,"E11.8.9.0"),sQuery(id+"F0.wireOp",EDGE,"E11.9.9.0"),sQuery(id+"F0.wireOp",EDGE,"E11.17.9.0"),sQuery(id+"F0.wireOp",EDGE,"E11.19.9.0"),sQuery(id+"F0.wireOp",EDGE,"E11.23.9.0"),sQuery(id+"F0.wireOp",EDGE,"E11.25.9.0"),sQuery(id+"F0.wireOp",EDGE,"E11.27.9.0"),sQuery(id+"F0.wireOp",EDGE,"E11.29.9.0"),sQuery(id+"F0.wireOp",EDGE,"E11.3.10.0"),sQuery(id+"F0.wireOp",EDGE,"E11.7.10.0"),sQuery(id+"F0.wireOp",EDGE,"E11.8.10.0"),sQuery(id+"F0.wireOp",EDGE,"E11.9.10.0"),sQuery(id+"F0.wireOp",EDGE,"E11.17.10.0"),sQuery(id+"F0.wireOp",EDGE,"E11.19.10.0"),sQuery(id+"F0.wireOp",EDGE,"E11.23.10.0"),sQuery(id+"F0.wireOp",EDGE,"E11.25.10.0"),sQuery(id+"F0.wireOp",EDGE,"E11.27.10.0"),sQuery(id+"F0.wireOp",EDGE,"E11.29.10.0"),sQuery(id+"F0.wireOp",EDGE,"E11.3.11.0"),sQuery(id+"F0.wireOp",EDGE,"E11.7.11.0"),sQuery(id+"F0.wireOp",EDGE,"E11.8.11.0"),sQuery(id+"F0.wireOp",EDGE,"E11.9.11.0"),sQuery(id+"F0.wireOp",EDGE,"E11.17.11.0"),sQuery(id+"F0.wireOp",EDGE,"E11.19.11.0"),sQuery(id+"F0.wireOp",EDGE,"E11.23.11.0"),sQuery(id+"F0.wireOp",EDGE,"E11.25.11.0"),sQuery(id+"F0.wireOp",EDGE,"E11.27.11.0"),sQuery(id+"F0.wireOp",EDGE,"E11.29.11.0"),sQuery(id+"F0.wireOp",EDGE,"E11.3.12.0"),sQuery(id+"F0.wireOp",EDGE,"E11.7.12.0"),sQuery(id+"F0.wireOp",EDGE,"E11.8.12.0"),sQuery(id+"F0.wireOp",EDGE,"E11.9.12.0"),sQuery(id+"F0.wireOp",EDGE,"E11.17.12.0"),sQuery(id+"F0.wireOp",EDGE,"E11.19.12.0"),sQuery(id+"F0.wireOp",EDGE,"E11.23.12.0"),sQuery(id+"F0.wireOp",EDGE,"E11.25.12.0"),sQuery(id+"F0.wireOp",EDGE,"E11.27.12.0"),sQuery(id+"F0.wireOp",EDGE,"E11.29.12.0"),sQuery(id+"F0.wireOp",EDGE,"E11.3.13.0"),sQuery(id+"F0.wireOp",EDGE,"E11.7.13.0"),sQuery(id+"F0.wireOp",EDGE,"E11.8.13.0"),sQuery(id+"F0.wireOp",EDGE,"E11.9.13.0"),sQuery(id+"F0.wireOp",EDGE,"E11.17.13.0"),sQuery(id+"F0.wireOp",EDGE,"E11.19.13.0"),sQuery(id+"F0.wireOp",EDGE,"E11.23.13.0"),sQuery(id+"F0.wireOp",EDGE,"E11.25.13.0"),sQuery(id+"F0.wireOp",EDGE,"E11.27.13.0"),sQuery(id+"F0.wireOp",EDGE,"E11.29.13.0"),sQuery(id+"F0.wireOp",EDGE,"E11.3.14.0"),sQuery(id+"F0.wireOp",EDGE,"E11.7.14.0"),sQuery(id+"F0.wireOp",EDGE,"E11.8.14.0"),sQuery(id+"F0.wireOp",EDGE,"E11.9.14.0"),sQuery(id+"F0.wireOp",EDGE,"E11.17.14.0"),sQuery(id+"F0.wireOp",EDGE,"E11.19.14.0"),sQuery(id+"F0.wireOp",EDGE,"E11.23.14.0"),sQuery(id+"F0.wireOp",EDGE,"E11.25.14.0"),sQuery(id+"F0.wireOp",EDGE,"E11.27.14.0"),sQuery(id+"F0.wireOp",EDGE,"E11.29.14.0"),sQuery(id+"F0.wireOp",EDGE,"E11.3.15.0"),sQuery(id+"F0.wireOp",EDGE,"E11.7.15.0"),sQuery(id+"F0.wireOp",EDGE,"E11.8.15.0"),sQuery(id+"F0.wireOp",EDGE,"E11.9.15.0"),sQuery(id+"F0.wireOp",EDGE,"E11.17.15.0"),sQuery(id+"F0.wireOp",EDGE,"E11.19.15.0"),sQuery(id+"F0.wireOp",EDGE,"E11.23.15.0"),sQuery(id+"F0.wireOp",EDGE,"E11.25.15.0"),sQuery(id+"F0.wireOp",EDGE,"E11.27.15.0"),sQuery(id+"F0.wireOp",EDGE,"E11.29.15.0"),sQuery(id+"F0.wireOp",EDGE,"E12")])],"isStart":false});
            var sketch = newSketch(context, id + "F2", { "sketchPlane" : qUnion([Q0])});
            skLineSegment(sketch, "E14.bottom", {"start": v(-0.5, 0) * mm, "end": v(0.5, 0) * mm});
            skLineSegment(sketch, "E14.top", {"start": v(-0.5, 36.96) * mm, "end": v(0.5, 36.96) * mm});
            skLineSegment(sketch, "E14.left", {"start": v(-0.5, 0) * mm, "end": v(-0.5, 36.96) * mm});
            skLineSegment(sketch, "E14.right", {"start": v(0.5, 0) * mm, "end": v(0.5, 36.96) * mm});
            skLineSegment(sketch, "E15.1.0", {"start": v(0, -0.5) * mm, "end": v(-36.96, -0.5) * mm});
            skLineSegment(sketch, "E15.1.1", {"start": v(0, 0.5) * mm, "end": v(-36.96, 0.5) * mm});
            skLineSegment(sketch, "E15.1.2", {"start": v(0, -0.5) * mm, "end": v(0, 0.5) * mm});
            skLineSegment(sketch, "E15.1.3", {"start": v(-36.96, -0.5) * mm, "end": v(-36.96, 0.5) * mm});
            skLineSegment(sketch, "E15.2.0", {"start": v(0.5, 0) * mm, "end": v(0.5, -36.96) * mm});
            skLineSegment(sketch, "E15.2.1", {"start": v(-0.5, 0) * mm, "end": v(-0.5, -36.96) * mm});
            skLineSegment(sketch, "E15.2.2", {"start": v(0.5, 0) * mm, "end": v(-0.5, 0) * mm});
            skLineSegment(sketch, "E15.2.3", {"start": v(0.5, -36.96) * mm, "end": v(-0.5, -36.96) * mm});
            skPoint(sketch, "E15.center", {"position": v(0, 0) * mm});
            skLineSegment(sketch, "E16.1.3.0", {"start": v(0, 0.5) * mm, "end": v(36.96, 0.5) * mm});
            skLineSegment(sketch, "E16.3.3.0", {"start": v(0, -0.5) * mm, "end": v(36.96, -0.5) * mm});
            skLineSegment(sketch, "E16.6.3.0", {"start": v(0, 0.5) * mm, "end": v(0, -0.5) * mm});
            skLineSegment(sketch, "E16.9.3.0", {"start": v(36.96, 0.5) * mm, "end": v(36.96, -0.5) * mm});
            skSolve(sketch);
        }
        {
            var Q0;
            Q0 = qSketchRegion(id + "F2", true);
            extrude(context, id + "F3", {"entities" : qUnion([Q0]), "operationType" : NewBodyOperationType.REMOVE, "oppositeDirection" : true, "depth" : .1 * mm});
        }
        {
            var Q0;
            Q0=makeQuery(id+"F1.opExtrude","CAP_FACE",FACE,{"disambiguationData":[OSD([sQuery(id+"F0.wireOp",EDGE,"E0"),sQuery(id+"F0.wireOp",EDGE,"E2.bottom"),sQuery(id+"F0.wireOp",EDGE,"E2.top"),sQuery(id+"F0.wireOp",EDGE,"E2.left"),sQuery(id+"F0.wireOp",EDGE,"E2.right"),sQuery(id+"F0.wireOp",EDGE,"E3"),sQuery(id+"F0.wireOp",EDGE,"E5.2.0"),sQuery(id+"F0.wireOp",EDGE,"E6"),sQuery(id+"F0.wireOp",EDGE,"E7"),sQuery(id+"F0.wireOp",EDGE,"E8"),sQuery(id+"F0.wireOp",EDGE,"E9"),sQuery(id+"F0.wireOp",EDGE,"E10.1.0"),sQuery(id+"F0.wireOp",EDGE,"E10.1.1"),sQuery(id+"F0.wireOp",EDGE,"E10.1.3"),sQuery(id+"F0.wireOp",EDGE,"E10.1.4"),sQuery(id+"F0.wireOp",EDGE,"E10.1.7"),sQuery(id+"F0.wireOp",EDGE,"E10.1.8"),sQuery(id+"F0.wireOp",EDGE,"E10.1.10"),sQuery(id+"F0.wireOp",EDGE,"E10.1.11"),sQuery(id+"F0.wireOp",EDGE,"E10.1.12"),sQuery(id+"F0.wireOp",EDGE,"E10.1.13"),sQuery(id+"F0.wireOp",EDGE,"E10.2.0"),sQuery(id+"F0.wireOp",EDGE,"E10.2.1"),sQuery(id+"F0.wireOp",EDGE,"E10.2.3"),sQuery(id+"F0.wireOp",EDGE,"E10.2.4"),sQuery(id+"F0.wireOp",EDGE,"E10.2.7"),sQuery(id+"F0.wireOp",EDGE,"E10.2.8"),sQuery(id+"F0.wireOp",EDGE,"E10.2.10"),sQuery(id+"F0.wireOp",EDGE,"E10.2.11"),sQuery(id+"F0.wireOp",EDGE,"E10.2.12"),sQuery(id+"F0.wireOp",EDGE,"E10.2.13"),sQuery(id+"F0.wireOp",EDGE,"E11.3.3.0"),sQuery(id+"F0.wireOp",EDGE,"E11.7.3.0"),sQuery(id+"F0.wireOp",EDGE,"E11.8.3.0"),sQuery(id+"F0.wireOp",EDGE,"E11.9.3.0"),sQuery(id+"F0.wireOp",EDGE,"E11.17.3.0"),sQuery(id+"F0.wireOp",EDGE,"E11.19.3.0"),sQuery(id+"F0.wireOp",EDGE,"E11.23.3.0"),sQuery(id+"F0.wireOp",EDGE,"E11.25.3.0"),sQuery(id+"F0.wireOp",EDGE,"E11.27.3.0"),sQuery(id+"F0.wireOp",EDGE,"E11.29.3.0"),sQuery(id+"F0.wireOp",EDGE,"E11.3.4.0"),sQuery(id+"F0.wireOp",EDGE,"E11.7.4.0"),sQuery(id+"F0.wireOp",EDGE,"E11.8.4.0"),sQuery(id+"F0.wireOp",EDGE,"E11.9.4.0"),sQuery(id+"F0.wireOp",EDGE,"E11.17.4.0"),sQuery(id+"F0.wireOp",EDGE,"E11.19.4.0"),sQuery(id+"F0.wireOp",EDGE,"E11.23.4.0"),sQuery(id+"F0.wireOp",EDGE,"E11.25.4.0"),sQuery(id+"F0.wireOp",EDGE,"E11.27.4.0"),sQuery(id+"F0.wireOp",EDGE,"E11.29.4.0"),sQuery(id+"F0.wireOp",EDGE,"E11.3.5.0"),sQuery(id+"F0.wireOp",EDGE,"E11.7.5.0"),sQuery(id+"F0.wireOp",EDGE,"E11.8.5.0"),sQuery(id+"F0.wireOp",EDGE,"E11.9.5.0"),sQuery(id+"F0.wireOp",EDGE,"E11.17.5.0"),sQuery(id+"F0.wireOp",EDGE,"E11.19.5.0"),sQuery(id+"F0.wireOp",EDGE,"E11.23.5.0"),sQuery(id+"F0.wireOp",EDGE,"E11.25.5.0"),sQuery(id+"F0.wireOp",EDGE,"E11.27.5.0"),sQuery(id+"F0.wireOp",EDGE,"E11.29.5.0"),sQuery(id+"F0.wireOp",EDGE,"E11.3.6.0"),sQuery(id+"F0.wireOp",EDGE,"E11.7.6.0"),sQuery(id+"F0.wireOp",EDGE,"E11.8.6.0"),sQuery(id+"F0.wireOp",EDGE,"E11.9.6.0"),sQuery(id+"F0.wireOp",EDGE,"E11.17.6.0"),sQuery(id+"F0.wireOp",EDGE,"E11.19.6.0"),sQuery(id+"F0.wireOp",EDGE,"E11.23.6.0"),sQuery(id+"F0.wireOp",EDGE,"E11.25.6.0"),sQuery(id+"F0.wireOp",EDGE,"E11.27.6.0"),sQuery(id+"F0.wireOp",EDGE,"E11.29.6.0"),sQuery(id+"F0.wireOp",EDGE,"E11.3.7.0"),sQuery(id+"F0.wireOp",EDGE,"E11.7.7.0"),sQuery(id+"F0.wireOp",EDGE,"E11.8.7.0"),sQuery(id+"F0.wireOp",EDGE,"E11.9.7.0"),sQuery(id+"F0.wireOp",EDGE,"E11.17.7.0"),sQuery(id+"F0.wireOp",EDGE,"E11.19.7.0"),sQuery(id+"F0.wireOp",EDGE,"E11.23.7.0"),sQuery(id+"F0.wireOp",EDGE,"E11.25.7.0"),sQuery(id+"F0.wireOp",EDGE,"E11.27.7.0"),sQuery(id+"F0.wireOp",EDGE,"E11.29.7.0"),sQuery(id+"F0.wireOp",EDGE,"E11.3.8.0"),sQuery(id+"F0.wireOp",EDGE,"E11.7.8.0"),sQuery(id+"F0.wireOp",EDGE,"E11.8.8.0"),sQuery(id+"F0.wireOp",EDGE,"E11.9.8.0"),sQuery(id+"F0.wireOp",EDGE,"E11.17.8.0"),sQuery(id+"F0.wireOp",EDGE,"E11.19.8.0"),sQuery(id+"F0.wireOp",EDGE,"E11.23.8.0"),sQuery(id+"F0.wireOp",EDGE,"E11.25.8.0"),sQuery(id+"F0.wireOp",EDGE,"E11.27.8.0"),sQuery(id+"F0.wireOp",EDGE,"E11.29.8.0"),sQuery(id+"F0.wireOp",EDGE,"E11.3.9.0"),sQuery(id+"F0.wireOp",EDGE,"E11.7.9.0"),sQuery(id+"F0.wireOp",EDGE,"E11.8.9.0"),sQuery(id+"F0.wireOp",EDGE,"E11.9.9.0"),sQuery(id+"F0.wireOp",EDGE,"E11.17.9.0"),sQuery(id+"F0.wireOp",EDGE,"E11.19.9.0"),sQuery(id+"F0.wireOp",EDGE,"E11.23.9.0"),sQuery(id+"F0.wireOp",EDGE,"E11.25.9.0"),sQuery(id+"F0.wireOp",EDGE,"E11.27.9.0"),sQuery(id+"F0.wireOp",EDGE,"E11.29.9.0"),sQuery(id+"F0.wireOp",EDGE,"E11.3.10.0"),sQuery(id+"F0.wireOp",EDGE,"E11.7.10.0"),sQuery(id+"F0.wireOp",EDGE,"E11.8.10.0"),sQuery(id+"F0.wireOp",EDGE,"E11.9.10.0"),sQuery(id+"F0.wireOp",EDGE,"E11.17.10.0"),sQuery(id+"F0.wireOp",EDGE,"E11.19.10.0"),sQuery(id+"F0.wireOp",EDGE,"E11.23.10.0"),sQuery(id+"F0.wireOp",EDGE,"E11.25.10.0"),sQuery(id+"F0.wireOp",EDGE,"E11.27.10.0"),sQuery(id+"F0.wireOp",EDGE,"E11.29.10.0"),sQuery(id+"F0.wireOp",EDGE,"E11.3.11.0"),sQuery(id+"F0.wireOp",EDGE,"E11.7.11.0"),sQuery(id+"F0.wireOp",EDGE,"E11.8.11.0"),sQuery(id+"F0.wireOp",EDGE,"E11.9.11.0"),sQuery(id+"F0.wireOp",EDGE,"E11.17.11.0"),sQuery(id+"F0.wireOp",EDGE,"E11.19.11.0"),sQuery(id+"F0.wireOp",EDGE,"E11.23.11.0"),sQuery(id+"F0.wireOp",EDGE,"E11.25.11.0"),sQuery(id+"F0.wireOp",EDGE,"E11.27.11.0"),sQuery(id+"F0.wireOp",EDGE,"E11.29.11.0"),sQuery(id+"F0.wireOp",EDGE,"E11.3.12.0"),sQuery(id+"F0.wireOp",EDGE,"E11.7.12.0"),sQuery(id+"F0.wireOp",EDGE,"E11.8.12.0"),sQuery(id+"F0.wireOp",EDGE,"E11.9.12.0"),sQuery(id+"F0.wireOp",EDGE,"E11.17.12.0"),sQuery(id+"F0.wireOp",EDGE,"E11.19.12.0"),sQuery(id+"F0.wireOp",EDGE,"E11.23.12.0"),sQuery(id+"F0.wireOp",EDGE,"E11.25.12.0"),sQuery(id+"F0.wireOp",EDGE,"E11.27.12.0"),sQuery(id+"F0.wireOp",EDGE,"E11.29.12.0"),sQuery(id+"F0.wireOp",EDGE,"E11.3.13.0"),sQuery(id+"F0.wireOp",EDGE,"E11.7.13.0"),sQuery(id+"F0.wireOp",EDGE,"E11.8.13.0"),sQuery(id+"F0.wireOp",EDGE,"E11.9.13.0"),sQuery(id+"F0.wireOp",EDGE,"E11.17.13.0"),sQuery(id+"F0.wireOp",EDGE,"E11.19.13.0"),sQuery(id+"F0.wireOp",EDGE,"E11.23.13.0"),sQuery(id+"F0.wireOp",EDGE,"E11.25.13.0"),sQuery(id+"F0.wireOp",EDGE,"E11.27.13.0"),sQuery(id+"F0.wireOp",EDGE,"E11.29.13.0"),sQuery(id+"F0.wireOp",EDGE,"E11.3.14.0"),sQuery(id+"F0.wireOp",EDGE,"E11.7.14.0"),sQuery(id+"F0.wireOp",EDGE,"E11.8.14.0"),sQuery(id+"F0.wireOp",EDGE,"E11.9.14.0"),sQuery(id+"F0.wireOp",EDGE,"E11.17.14.0"),sQuery(id+"F0.wireOp",EDGE,"E11.19.14.0"),sQuery(id+"F0.wireOp",EDGE,"E11.23.14.0"),sQuery(id+"F0.wireOp",EDGE,"E11.25.14.0"),sQuery(id+"F0.wireOp",EDGE,"E11.27.14.0"),sQuery(id+"F0.wireOp",EDGE,"E11.29.14.0"),sQuery(id+"F0.wireOp",EDGE,"E11.3.15.0"),sQuery(id+"F0.wireOp",EDGE,"E11.7.15.0"),sQuery(id+"F0.wireOp",EDGE,"E11.8.15.0"),sQuery(id+"F0.wireOp",EDGE,"E11.9.15.0"),sQuery(id+"F0.wireOp",EDGE,"E11.17.15.0"),sQuery(id+"F0.wireOp",EDGE,"E11.19.15.0"),sQuery(id+"F0.wireOp",EDGE,"E11.23.15.0"),sQuery(id+"F0.wireOp",EDGE,"E11.25.15.0"),sQuery(id+"F0.wireOp",EDGE,"E11.27.15.0"),sQuery(id+"F0.wireOp",EDGE,"E11.29.15.0"),sQuery(id+"F0.wireOp",EDGE,"E12")])],"isStart":false});
            chamfer(context, id + "F4", {"entities" : qUnion([Q0]), "width" : .25 * mm, "tangentPropagation" : true});
        }
    });
